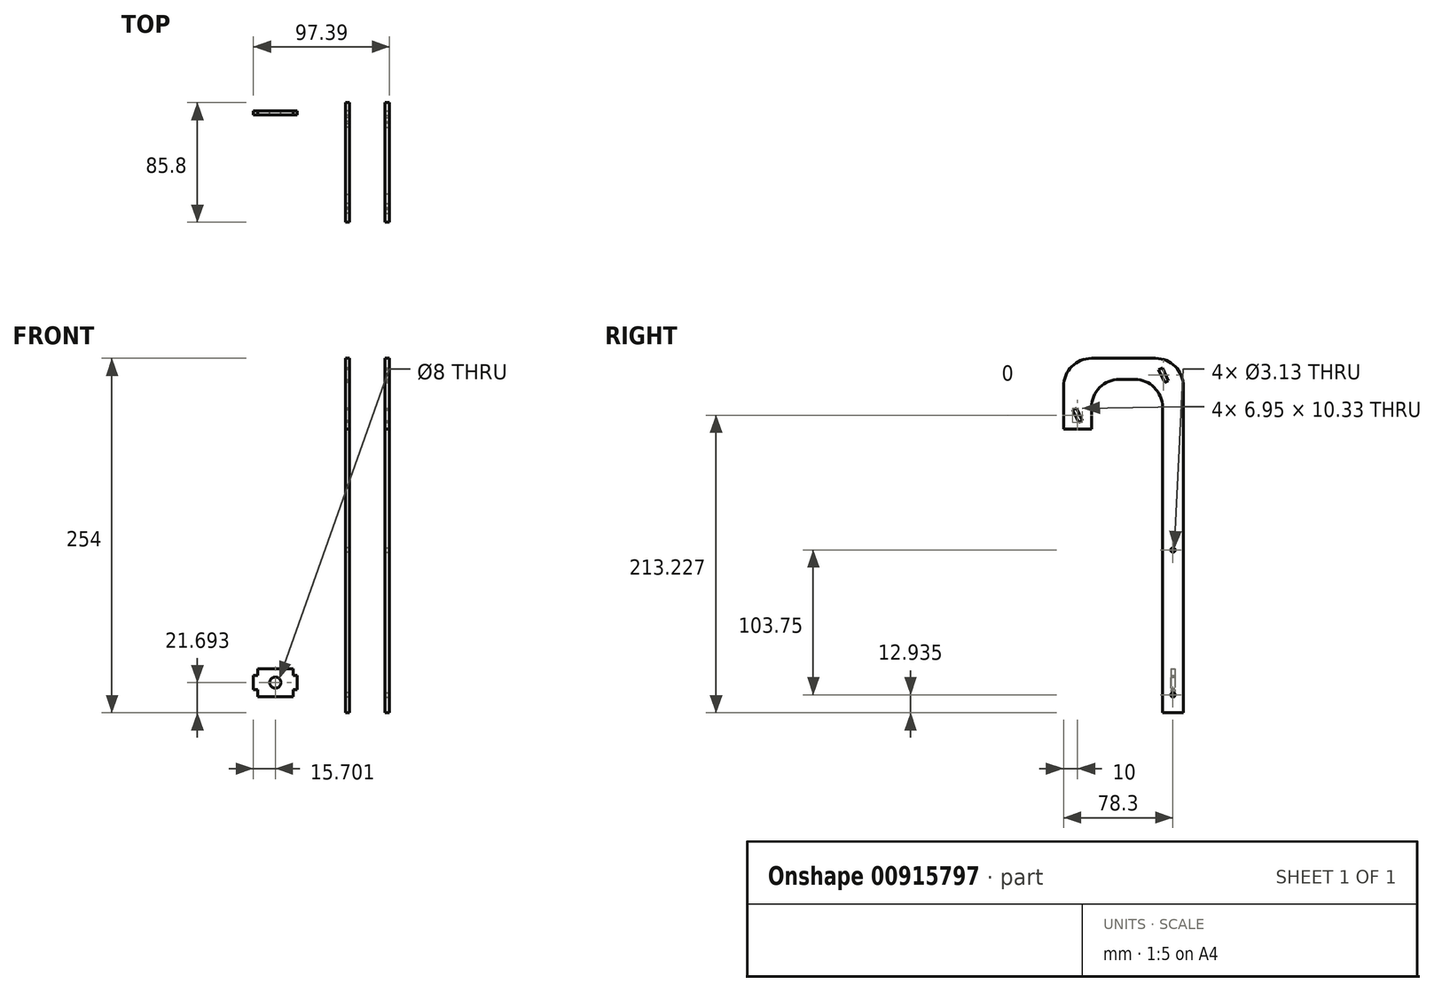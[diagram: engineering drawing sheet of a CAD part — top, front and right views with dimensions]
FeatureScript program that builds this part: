
annotation { "Feature Type Name" : "Feature", "Feature Type Description" : "" }
export const myFeature = defineFeature(function(context is Context, id is Id, definition is map)
    precondition{}
    {
        {
            var Q0;
            Q0=qCreatedBy(makeId("Right.planeOp"),FACE);
            cPlane(context, id + "F0", {"entities" : qUnion([Q0]), "cplaneType" : CPlaneType.OFFSET, "offset" : 12.7 * mm, "width" : 150 * mm, "height" : 150 * mm});
        }
        {
            var Q0;
            Q0=qCreatedBy(id+"F0.planeOp",FACE);
            var sketch = newSketch(context, id + "F1", { "sketchPlane" : qUnion([Q0])});
            skLineSegment(sketch, "E0", {"start": v(0, 0) * mm, "end": v(15, 0) * mm});
            skLineSegment(sketch, "E1", {"start": v(15, 0) * mm, "end": v(15, 254) * mm});
            skLineSegment(sketch, "E2", {"start": v(15, 254) * mm, "end": v(-70.8, 254) * mm});
            skLineSegment(sketch, "E3", {"start": v(-70.8, 254) * mm, "end": v(-70.8, 203.2) * mm});
            skLineSegment(sketch, "E4", {"start": v(-70.8, 203.2) * mm, "end": v(-50.8, 203.2) * mm});
            skLineSegment(sketch, "E5", {"start": v(-50.8, 203.2) * mm, "end": v(-50.8, 239) * mm});
            skLineSegment(sketch, "E6", {"start": v(-50.8, 239) * mm, "end": v(0, 239) * mm});
            skLineSegment(sketch, "E7", {"start": v(0, 239) * mm, "end": v(0, 0) * mm});
            skSolve(sketch);
        }
        {
            var Q0;
            Q0 = qSketchRegion(id + "F1", true);
            extrude(context, id + "F2", {"entities" : qUnion([Q0]), "depth" : 3 * mm, "offsetDistance" : 25 * mm});
        }
        {
            var Q0;
            Q0=makeQuery(id+"F2.opExtrude","SWEPT_EDGE",EDGE,{"disambiguationData":[OSD([sQuery(id+"F1.wireOp",EDGE,"E2"),sQuery(id+"F1.wireOp",EDGE,"E3")])]});
            var Q1;
            Q1=makeQuery(id+"F2.opExtrude","SWEPT_EDGE",EDGE,{"disambiguationData":[OSD([sQuery(id+"F1.wireOp",EDGE,"E1"),sQuery(id+"F1.wireOp",EDGE,"E2")])]});
            var Q2;
            Q2=makeQuery(id+"F2.opExtrude","SWEPT_EDGE",EDGE,{"disambiguationData":[OSD([sQuery(id+"F1.wireOp",EDGE,"E5"),sQuery(id+"F1.wireOp",EDGE,"E6")])]});
            var Q3;
            Q3=makeQuery(id+"F2.opExtrude","SWEPT_EDGE",EDGE,{"disambiguationData":[OSD([sQuery(id+"F1.wireOp",EDGE,"E6"),sQuery(id+"F1.wireOp",EDGE,"E7")])]});
            fillet(context, id + "F3", {"entities" : qUnion([Q0, Q1, Q2, Q3]), "radius" : 20 * mm, "tangentPropagation" : true, "allowEdgeOverflow" : false});
        }
        {
            var Q0;
            Q0=makeQuery(id+"F2.opExtrude","CAP_FACE",FACE,{"disambiguationData":[OSD([sQuery(id+"F1.wireOp",EDGE,"E0"),sQuery(id+"F1.wireOp",EDGE,"E1"),sQuery(id+"F1.wireOp",EDGE,"E2"),sQuery(id+"F1.wireOp",EDGE,"E3"),sQuery(id+"F1.wireOp",EDGE,"E4"),sQuery(id+"F1.wireOp",EDGE,"E5"),sQuery(id+"F1.wireOp",EDGE,"E6"),sQuery(id+"F1.wireOp",EDGE,"E7")])],"isStart":false});
            var sketch = newSketch(context, id + "F4", { "sketchPlane" : qUnion([Q0])});
            skCircle(sketch, "E8", {"center": v(7.5, 12.94) * mm, "radius": 1.56 * mm});
            skCircle(sketch, "E9", {"center": v(7.5, 116.69) * mm, "radius": 1.56 * mm});
            skSolve(sketch);
        }
        {
            var Q0;
            Q0 = qSketchRegion(id + "F4", true);
            extrude(context, id + "F5", {"entities" : qUnion([Q0]), "operationType" : NewBodyOperationType.REMOVE, "oppositeDirection" : true, "depth" : 25 * mm, "offsetDistance" : 25 * mm});
        }
        {
            var Q0;
            Q0=makeQuery(id+"F2.opExtrude","CAP_FACE",FACE,{"disambiguationData":[OSD([sQuery(id+"F1.wireOp",EDGE,"E0"),sQuery(id+"F1.wireOp",EDGE,"E1"),sQuery(id+"F1.wireOp",EDGE,"E2"),sQuery(id+"F1.wireOp",EDGE,"E3"),sQuery(id+"F1.wireOp",EDGE,"E4"),sQuery(id+"F1.wireOp",EDGE,"E5"),sQuery(id+"F1.wireOp",EDGE,"E6"),sQuery(id+"F1.wireOp",EDGE,"E7")])],"isStart":false});
            var sketch = newSketch(context, id + "F6", { "sketchPlane" : qUnion([Q0])});
            skLineSegment(sketch, "E10", {"start": v(-2.72, 245.83) * mm, "end": v(0, 247.1) * mm});
            skLineSegment(sketch, "E11", {"start": v(0, 247.1) * mm, "end": v(4.23, 238.03) * mm});
            skLineSegment(sketch, "E12", {"start": v(4.23, 238.03) * mm, "end": v(1.5, 236.76) * mm});
            skLineSegment(sketch, "E13", {"start": v(1.5, 236.76) * mm, "end": v(-2.72, 245.83) * mm});
            skLineSegment(sketch, "E14", {"start": v(-0.6, 241.3) * mm, "end": v(-75.65, 206.3) * mm, "construction": true});
            skLineSegment(sketch, "E15.bottom", {"start": v(-64.27, 217.13) * mm, "end": v(-61.55, 218.4) * mm});
            skLineSegment(sketch, "E15.top", {"start": v(-60.05, 208.06) * mm, "end": v(-57.33, 209.33) * mm});
            skLineSegment(sketch, "E15.left", {"start": v(-64.27, 217.13) * mm, "end": v(-60.05, 208.06) * mm});
            skLineSegment(sketch, "E15.right", {"start": v(-61.55, 218.4) * mm, "end": v(-57.33, 209.33) * mm});
            skPoint(sketch, "E16", {"position": v(-59.44, 213.86) * mm});
            skLineSegment(sketch, "E17", {"start": v(-61.55, 218.4) * mm, "end": v(-60.05, 208.06) * mm, "construction": true});
            skPoint(sketch, "E18", {"position": v(-60.8, 213.23) * mm});
            skSolve(sketch);
        }
        {
            var Q0;
            Q0 = qSketchRegion(id + "F6", true);
            extrude(context, id + "F7", {"entities" : qUnion([Q0]), "operationType" : NewBodyOperationType.REMOVE, "oppositeDirection" : true, "depth" : 25 * mm, "offsetDistance" : 25 * mm});
        }
        {
            var Q0;
            Q0=makeQuery(id+"F2.opExtrude","SWEPT_BODY",BODY,{"disambiguationData":[OSD([sQuery(id+"F1.wireOp",EDGE,"E0"),sQuery(id+"F1.wireOp",EDGE,"E1"),sQuery(id+"F1.wireOp",EDGE,"E2"),sQuery(id+"F1.wireOp",EDGE,"E3"),sQuery(id+"F1.wireOp",EDGE,"E4"),sQuery(id+"F1.wireOp",EDGE,"E5"),sQuery(id+"F1.wireOp",EDGE,"E6"),sQuery(id+"F1.wireOp",EDGE,"E7")])]});
            var Q1;
            Q1=qCreatedBy(makeId("Right.planeOp"),FACE);
            mirror(context, id + "F8", {"entities" : qUnion([Q0]), "mirrorPlane" : qUnion([Q1])});
        }
        {
            var Q0;
            Q0=qCreatedBy(makeId("Front.planeOp"),FACE);
            cPlane(context, id + "F9", {"entities" : qUnion([Q0]), "cplaneType" : CPlaneType.OFFSET, "offset" : 9 * mm, "oppositeDirection" : true, "width" : 150 * mm, "height" : 150 * mm});
        }
        {
            var Q0;
            Q0=qCreatedBy(id+"F9.planeOp",FACE);
            var sketch = newSketch(context, id + "F10", { "sketchPlane" : qUnion([Q0])});
            skLineSegment(sketch, "E19.bottom", {"start": v(-53.29, 31.7) * mm, "end": v(-78.69, 31.7) * mm});
            skLineSegment(sketch, "E19.top", {"start": v(-53.29, 11.7) * mm, "end": v(-78.69, 11.7) * mm});
            skLineSegment(sketch, "E19.left", {"start": v(-53.29, 31.7) * mm, "end": v(-53.29, 11.7) * mm});
            skLineSegment(sketch, "E19.right", {"start": v(-78.69, 31.7) * mm, "end": v(-78.69, 11.7) * mm});
            skLineSegment(sketch, "E20.bottom", {"start": v(-78.69, 26.7) * mm, "end": v(-81.69, 26.7) * mm});
            skLineSegment(sketch, "E20.top", {"start": v(-78.69, 16.7) * mm, "end": v(-81.69, 16.7) * mm});
            skLineSegment(sketch, "E20.left", {"start": v(-78.69, 26.7) * mm, "end": v(-78.69, 16.7) * mm});
            skLineSegment(sketch, "E20.right", {"start": v(-81.69, 26.7) * mm, "end": v(-81.69, 16.7) * mm});
            skLineSegment(sketch, "E21.bottom", {"start": v(-53.29, 26.7) * mm, "end": v(-50.29, 26.7) * mm});
            skLineSegment(sketch, "E21.top", {"start": v(-53.29, 16.7) * mm, "end": v(-50.29, 16.7) * mm});
            skLineSegment(sketch, "E21.left", {"start": v(-53.29, 26.7) * mm, "end": v(-53.29, 16.7) * mm});
            skLineSegment(sketch, "E21.right", {"start": v(-50.29, 26.7) * mm, "end": v(-50.29, 16.7) * mm});
            skPoint(sketch, "E22", {"position": v(-53.29, 21.7) * mm});
            skPoint(sketch, "E23", {"position": v(-50.29, 21.7) * mm});
            skSolve(sketch);
        }
        {
            var Q0;
            Q0 = qSketchRegion(id + "F10", true);
            extrude(context, id + "F11", {"entities" : qUnion([Q0]), "depth" : 3 * mm, "offsetDistance" : 25 * mm});
        }
        {
            var Q0;
            Q0=makeQuery(id+"F11.opExtrude","CAP_FACE",FACE,{"disambiguationData":[OSD([sQuery(id+"F10.wireOp",EDGE,"E19.bottom"),sQuery(id+"F10.wireOp",EDGE,"E19.top"),sQuery(id+"F10.wireOp",EDGE,"E19.left"),sQuery(id+"F10.wireOp",EDGE,"E19.right"),sQuery(id+"F10.wireOp",EDGE,"E20.bottom"),sQuery(id+"F10.wireOp",EDGE,"E20.top"),sQuery(id+"F10.wireOp",EDGE,"E20.right"),sQuery(id+"F10.wireOp",EDGE,"E21.bottom"),sQuery(id+"F10.wireOp",EDGE,"E21.top"),sQuery(id+"F10.wireOp",EDGE,"E21.right")])],"isStart":true});
            var sketch = newSketch(context, id + "F12", { "sketchPlane" : qUnion([Q0])});
            skCircle(sketch, "E24", {"center": v(65.99, 21.7) * mm, "radius": 4 * mm});
            skLineSegment(sketch, "E25", {"start": v(75.63, 31.7) * mm, "end": v(75.63, 11.7) * mm, "construction": true});
            skLineSegment(sketch, "E26", {"start": v(53.29, 13.43) * mm, "end": v(78.69, 13.43) * mm, "construction": true});
            skPoint(sketch, "E27", {"position": v(75.63, 21.7) * mm});
            skPoint(sketch, "E28", {"position": v(65.99, 13.43) * mm});
            skSolve(sketch);
        }
        {
            var Q0;
            Q0 = qSketchRegion(id + "F12", true);
            extrude(context, id + "F13", {"entities" : qUnion([Q0]), "operationType" : NewBodyOperationType.REMOVE, "oppositeDirection" : true, "depth" : 25 * mm, "offsetDistance" : 25 * mm});
        }
    });
